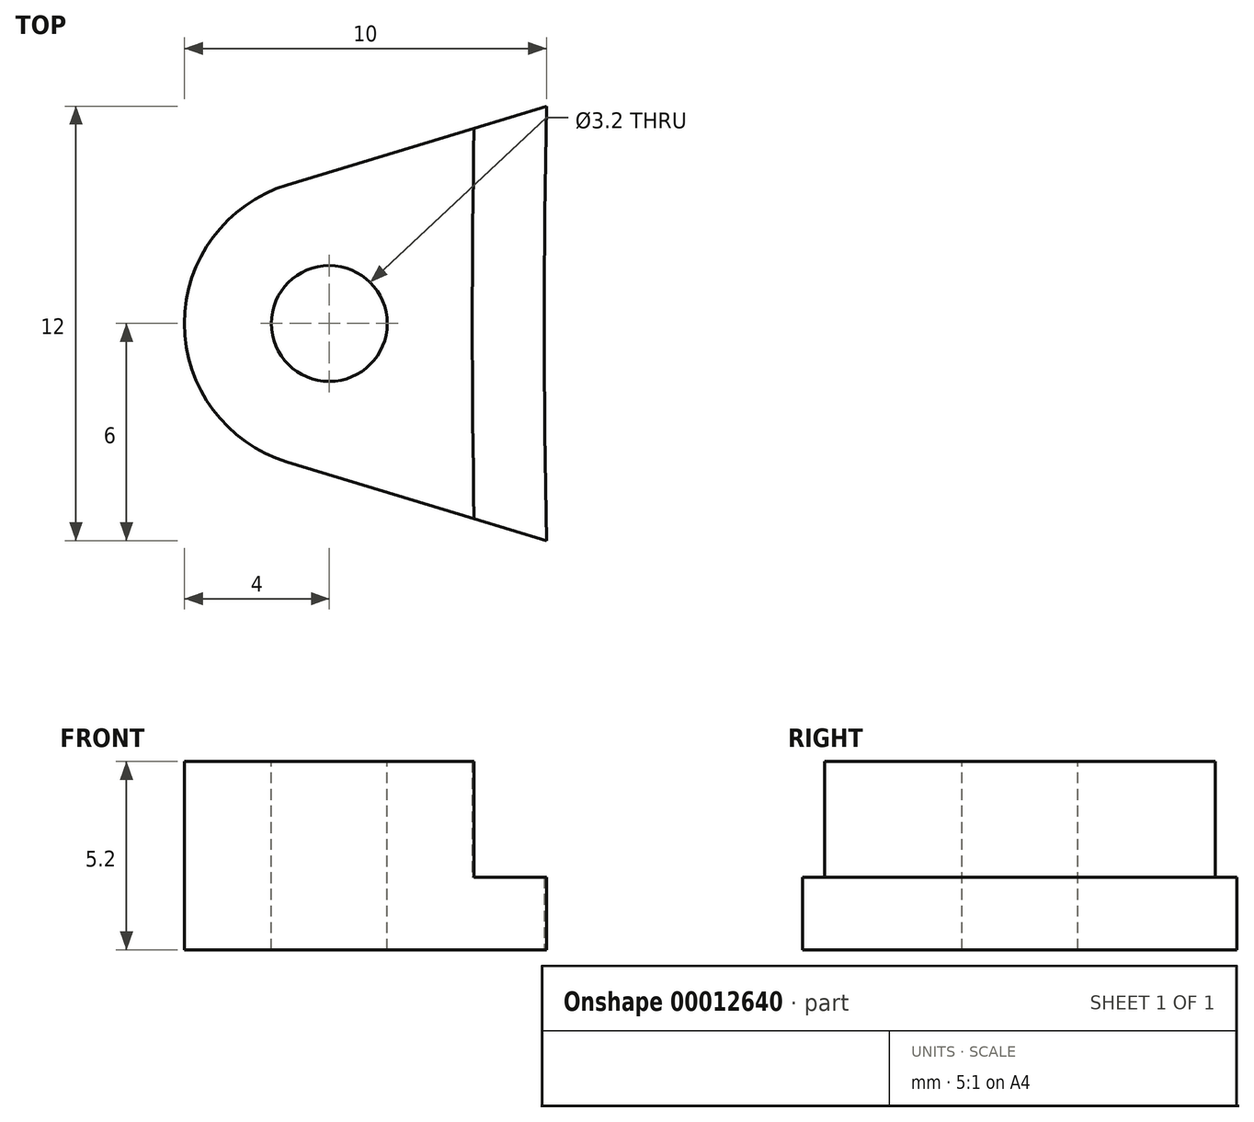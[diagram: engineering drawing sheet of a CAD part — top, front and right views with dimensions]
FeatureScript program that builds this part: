
annotation { "Feature Type Name" : "Feature", "Feature Type Description" : "" }
export const myFeature = defineFeature(function(context is Context, id is Id, definition is map)
    precondition{}
    {
        {
            var Q0;
            Q0=qCreatedBy(makeId("Top.planeOp"),FACE);
            var sketch = newSketch(context, id + "F0", { "sketchPlane" : qUnion([Q0])});
            skArc(sketch, "E0", {"start": v(-1.16, 3.83) * mm, "mid": v(-4, 0) * mm, "end": v(-1.16, -3.83) * mm});
            skArc(sketch, "E1", {"start": v(6, 6) * mm, "mid": v(5.94, 0) * mm, "end": v(6, -6) * mm});
            skLineSegment(sketch, "E2", {"start": v(6, 6) * mm, "end": v(-1.16, 3.83) * mm});
            skLineSegment(sketch, "E3", {"start": v(6, -6) * mm, "end": v(-1.16, -3.83) * mm});
            skSolve(sketch);
        }
        {
            var Q0;
            Q0=makeQuery(id+"F0.imprint","IMPRINT",FACE,{"disambiguationData":[TD([[makeQuery(id+"F0.imprint","IMPRINT",EDGE,{"derivedFrom":sQuery(id+"F0.wireOp",EDGE,"E0")}),1.0]])]});
            extrude(context, id + "F1", {"entities" : qUnion([Q0]), "depth" : 2 * mm});
        }
        {
            var Q0;
            Q0=makeQuery(id+"F1.opExtrude","CAP_FACE",FACE,{"disambiguationData":[OSD([sQuery(id+"F0.wireOp",EDGE,"E0"),sQuery(id+"F0.wireOp",EDGE,"E1"),sQuery(id+"F0.wireOp",EDGE,"E2"),sQuery(id+"F0.wireOp",EDGE,"E3")])],"isStart":false});
            var sketch = newSketch(context, id + "F2", { "sketchPlane" : qUnion([Q0])});
            skArc(sketch, "E4.1", {"start": v(-1.16, 3.83) * mm, "mid": v(-4, 0) * mm, "end": v(-1.16, -3.83) * mm});
            skArc(sketch, "E5", {"start": v(4, 5.4) * mm, "mid": v(3.95, 0) * mm, "end": v(4, -5.4) * mm});
            skLineSegment(sketch, "E6", {"start": v(-1.16, 3.83) * mm, "end": v(4, 5.4) * mm});
            skLineSegment(sketch, "E7", {"start": v(-1.16, -3.83) * mm, "end": v(4, -5.4) * mm});
            skSolve(sketch);
        }
        {
            var Q0;
            Q0 = qSketchRegion(id + "F2", true);
            extrude(context, id + "F3", {"entities" : qUnion([Q0]), "operationType" : NewBodyOperationType.ADD, "depth" : 3.2 * mm});
        }
        {
            var Q0;
            Q0=makeQuery(id+"F3.opExtrude","CAP_FACE",FACE,{"disambiguationData":[OSD([sQuery(id+"F2.wireOp",EDGE,"E4.1"),sQuery(id+"F2.wireOp",EDGE,"E5"),sQuery(id+"F2.wireOp",EDGE,"E6"),sQuery(id+"F2.wireOp",EDGE,"E7")])],"isStart":false});
            var sketch = newSketch(context, id + "F4", { "sketchPlane" : qUnion([Q0])});
            skCircle(sketch, "E8", {"center": v(0, 0) * mm, "radius": 1.6 * mm});
            skSolve(sketch);
        }
        {
            var Q0;
            Q0 = qSketchRegion(id + "F4", true);
            extrude(context, id + "F5", {"entities" : qUnion([Q0]), "operationType" : NewBodyOperationType.REMOVE, "endBound" : BoundingType.THROUGH_ALL, "oppositeDirection" : true, "depth" : 25 * mm});
        }
    });
